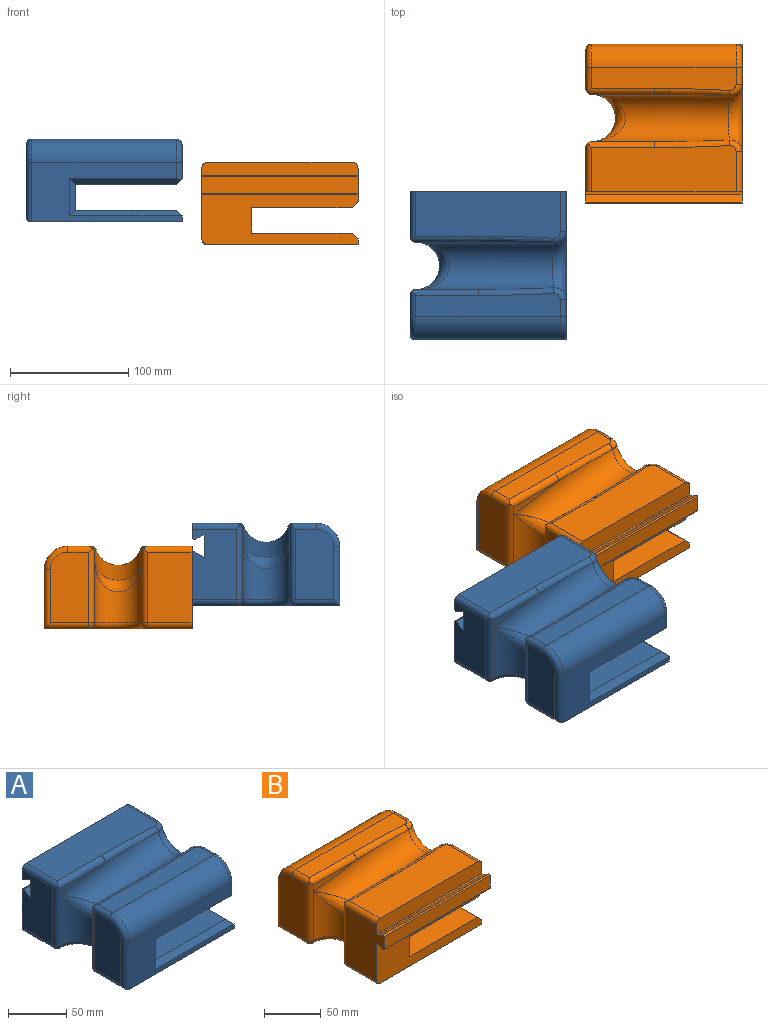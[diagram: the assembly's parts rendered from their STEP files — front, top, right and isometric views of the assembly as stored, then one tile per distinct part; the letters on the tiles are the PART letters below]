
ASSEMBLY  parts=2 mates=1
PART A: 55 faces, bbox 142.1x127.4x74.7 mm
  f0: plane 132x44.75mm, normal (0,1,0), area 3941.6mm2, adj f1,f45,f46,f47,f48,f49,f50,f51
  f1: cylinder r=5mm len=37.5mm, axis (0,1,0), area 294.5mm2, adj f0,f2,f45,f54
  f2: sphere r=5mm, area 39.3mm2, adj f1,f3,f44
  f3: cylinder r=5mm len=63.54mm, axis (0,0,1), area 485.1mm2, adj f2,f4,f41,f42,f43,f54
  f4: cylinder r=5mm len=56.8mm, axis (1,0,0), area 432.2mm2, adj f3,f5,f40,f41,f43
  f5: bspline ~110.14x7.38mm, area 440.2mm2, adj f4,f6,f29,f40
  f6: cylinder r=20mm len=118.3mm, axis (-0.99,0,-0.14), area 5823.8mm2, adj f5,f7,f26,f27,f28,f41
  f7: plane 53.26x7.68mm, normal (0,1,0), area 204.4mm2, adj f6,f8,f25
  f8: cylinder r=5mm len=56.8mm, axis (-1,0,0), area 432.2mm2, adj f7,f9,f24,f25,f26
  f9: plane 122.56x19.77mm, normal (0,0,1), area 2173.6mm2, adj f8,f10,f11,f23,f24,f26
  f10: bspline ~12.78x12.34mm, area 87.4mm2, adj f9,f11,f26,f27
  f11: cylinder r=5mm len=13.91mm, axis (0,1,0), area 109.3mm2, adj f9,f10,f12,f52
  f12: torus R=15mm, axis (1,0,0), area 224.3mm2, adj f11,f13,f23,f52
  f13: cylinder r=5mm len=14.96mm, axis (0,0,-1), area 111.8mm2, adj f12,f14,f17,f51,f52
  f14: plane 94.24x5.7mm, normal (0,-0.71,-0.71), area 632.6mm2, adj f13,f15,f17,f50,f51
  f15: plane 31.5x5mm, normal (0.71,-0.71,0), area 187.4mm2, adj f14,f16,f17,f49
  f16: plane 95x5mm, normal (0,-0.71,0.71), area 636.4mm2, adj f15,f17,f47,f48
  f17: plane 127x50mm, normal (0,-1,0), area 3290mm2, adj f13,f14,f15,f16,f18,f23,f45,f46
  f18: cylinder r=5mm len=50mm, axis (0,0,1), area 373.1mm2, adj f17,f19,f21,f22
  f19: cylinder r=5mm len=37.5mm, axis (0,1,0), area 274.9mm2, adj f18,f20,f21,f45
  f20: sphere r=5mm, area 25mm2, adj f19,f25,f44
  f21: plane 60x32.5mm, normal (-1,0,0), area 1901.7mm2, adj f18,f19,f22,f24,f25
  f22: torus R=15mm, axis (1,0,0), area 224.3mm2, adj f18,f21,f23,f24
  f23: cylinder r=20mm len=122mm, axis (1,0,0), area 3832.7mm2, adj f9,f12,f17,f22
  f24: cylinder r=5mm len=21.04mm, axis (0,-1,0), area 151.3mm2, adj f8,f9,f21,f22,f25
  f25: cylinder r=5mm len=63.54mm, axis (0,0,1), area 485.1mm2, adj f7,f8,f20,f21,f24,f42
  f26: bspline ~63.48x6.36mm, area 440.2mm2, adj f6,f8,f9,f10
  f27: bspline ~57.18x24.11mm, area 968.4mm2, adj f6,f10,f29,f52
  f28: bspline ~40x28.57mm, area 7.5mm2, adj f6,f42
  f29: bspline ~12.78x12.35mm, area 87.4mm2, adj f5,f27,f30,f40
  f30: cylinder r=5mm len=33.91mm, axis (0,1,0), area 266.3mm2, adj f29,f31,f40,f52
  f31: plane 132x13.25mm, normal (0,1,0), area 1738.3mm2, adj f30,f32,f40,f43,f52,f54
  f32: plane 132x1mm, normal (0,0.71,-0.71), area 186.7mm2, adj f31,f33,f52,f54
  f33: plane 132x0.73mm, normal (0,0,-1), area 96.6mm2, adj f32,f34,f52,f54
  f34: cylinder r=1mm len=132mm, axis (-1,0,0), area 69.1mm2, adj f33,f35,f52,f54
  f35: plane 132x8.43mm, normal (0,-0.5,-0.87), area 1284.6mm2, adj f34,f36,f52,f54
  f36: plane 132x20mm, normal (0,1,0), area 2640mm2, adj f35,f37,f52,f54
  f37: plane 132x8.43mm, normal (0,-0.5,0.87), area 1284.6mm2, adj f36,f38,f52,f54
  f38: cylinder r=1mm len=132mm, axis (1,0,0), area 69.1mm2, adj f37,f39,f52,f54
  f39: plane 132x0.73mm, normal (0,0,1), area 96.6mm2, adj f38,f52,f53,f54
  f40: plane 122.56x39.77mm, normal (0,0,1), area 4613.7mm2, adj f4,f5,f29,f30,f31,f43
  f41: plane 53.26x7.68mm, normal (0,-1,0), area 204.4mm2, adj f3,f4,f6
  f42: cylinder r=20mm len=52.32mm, axis (0,0,1), area 2248.2mm2, adj f3,f25,f28,f44
  f43: cylinder r=5mm len=41.04mm, axis (0,-1,0), area 308.4mm2, adj f3,f4,f31,f40,f54
  f44: torus R=25mm, axis (0,0,1), area 538.3mm2, adj f2,f20,f42,f45
  f45: plane 127x125mm, normal (0,0,-1), area 14893.3mm2, adj f0,f1,f17,f19,f44,f46
  f46: plane 125x5mm, normal (1,0,0), area 625mm2, adj f0,f17,f45,f47
  f47: plane 125x5mm, normal (0.71,0,0.71), area 866.2mm2, adj f0,f16,f46,f48
  f48: plane 120x85mm, normal (0,0,1), area 10200mm2, adj f0,f16,f47,f49
  f49: plane 120x21.5mm, normal (1,0,0), area 2580mm2, adj f0,f15,f48,f50
  f50: plane 120x85mm, normal (0,0,-1), area 10200mm2, adj f0,f14,f49,f51
  f51: plane 124.24x5.7mm, normal (0.71,0,-0.71), area 862.4mm2, adj f0,f13,f14,f50,f52
  f52: plane 120x28.5mm, normal (1,0,0), area 2335mm2, adj f0,f11,f12,f13,f27,f30,f31,f32
  f53: plane 132x1mm, normal (0,0.71,0.71), area 186.7mm2, adj f0,f39,f52,f54
  f54: plane 60x37.5mm, normal (-1,0,0), area 2099.1mm2, adj f0,f1,f3,f31,f32,f33,f34,f35
PART B: 53 faces, bbox 142.1x137.4x74.7 mm
  f0: plane 132x46.75mm, normal (0,-1,0), area 4205.6mm2, adj f1,f43,f44,f45,f46,f47,f48,f49
  f1: plane 124.24x5.7mm, normal (0.71,0,-0.71), area 862.4mm2, adj f0,f2,f42,f43,f52
  f2: cylinder r=5mm len=14.96mm, axis (0,0,1), area 111.8mm2, adj f1,f3,f39,f42,f52
  f3: torus R=15mm, axis (1,0,0), area 224.3mm2, adj f2,f4,f38,f52
  f4: cylinder r=5mm len=13.91mm, axis (0,1,0), area 109.3mm2, adj f3,f5,f37,f52
  f5: bspline ~12.78x12.35mm, area 87.4mm2, adj f4,f6,f36,f37
  f6: bspline ~57.18x24.11mm, area 968.4mm2, adj f5,f7,f35,f52
  f7: bspline ~12.78x12.34mm, area 87.4mm2, adj f6,f8,f33,f34
  f8: plane 122.56x39.77mm, normal (0,0,1), area 4613.6mm2, adj f7,f9,f16,f32,f33,f34
  f9: plane 132x15.25mm, normal (0,-1,0), area 2002.3mm2, adj f8,f10,f16,f34,f50,f52
  f10: plane 132x2mm, normal (0,0,1), area 264mm2, adj f9,f11,f50,f52
  f11: plane 132x6.5mm, normal (0,0.5,0.87), area 990.7mm2, adj f10,f12,f50,f52
  f12: cylinder r=1mm len=132mm, axis (-1,0,0), area 276.5mm2, adj f11,f13,f50,f52
  f13: plane 132x13.77mm, normal (0,-1,0), area 1818.1mm2, adj f12,f14,f50,f52
  f14: cylinder r=1mm len=132mm, axis (-1,0,0), area 276.5mm2, adj f13,f15,f50,f52
  f15: plane 132x6.5mm, normal (0,0.5,-0.87), area 990.7mm2, adj f14,f50,f51,f52
  f16: cylinder r=5mm len=41.04mm, axis (0,-1,0), area 308.4mm2, adj f8,f9,f17,f32,f50
  f17: cylinder r=5mm len=63.54mm, axis (0,0,1), area 485.1mm2, adj f16,f18,f29,f31,f32,f50
  f18: sphere r=5mm, area 25mm2, adj f17,f19,f49
  f19: torus R=25mm, axis (0,0,1), area 538.3mm2, adj f18,f20,f29,f48
  f20: sphere r=5mm, area 39.3mm2, adj f19,f21,f28
  f21: cylinder r=5mm len=37.5mm, axis (0,1,0), area 274.9mm2, adj f20,f22,f27,f48
  f22: cylinder r=5mm len=50mm, axis (0,0,-1), area 373.1mm2, adj f21,f23,f27,f39
  f23: torus R=15mm, axis (1,0,0), area 224.3mm2, adj f22,f24,f27,f38
  f24: cylinder r=5mm len=21.04mm, axis (0,-1,0), area 151.3mm2, adj f23,f25,f27,f28,f37
  f25: cylinder r=5mm len=56.8mm, axis (1,0,0), area 432.2mm2, adj f24,f26,f28,f36,f37
  f26: plane 53.26x7.68mm, normal (0,-1,0), area 204.4mm2, adj f25,f28,f35
  f27: plane 60x32.5mm, normal (-1,0,0), area 1901.7mm2, adj f21,f22,f23,f24,f28
  f28: cylinder r=5mm len=63.54mm, axis (0,0,1), area 485.1mm2, adj f20,f24,f25,f26,f27,f29
  f29: cylinder r=20mm len=52.32mm, axis (0,0,1), area 2248.2mm2, adj f17,f19,f28,f30
  f30: bspline ~40x28.57mm, area 7.5mm2, adj f29,f35
  f31: plane 53.26x7.68mm, normal (0,1,0), area 204.4mm2, adj f17,f32,f35
  f32: cylinder r=5mm len=56.8mm, axis (-1,0,0), area 432.2mm2, adj f8,f16,f17,f31,f33
  f33: bspline ~63.48x6.36mm, area 440.2mm2, adj f7,f8,f32,f35
  f34: cylinder r=5mm len=33.91mm, axis (0,1,0), area 266.3mm2, adj f7,f8,f9,f52
  f35: cylinder r=20mm len=118.3mm, axis (-0.99,0,-0.14), area 5823.8mm2, adj f6,f26,f30,f31,f33,f36
  f36: bspline ~110.14x7.38mm, area 440.2mm2, adj f5,f25,f35,f37
  f37: plane 122.56x19.77mm, normal (0,0,1), area 2173.7mm2, adj f4,f5,f24,f25,f36,f38
  f38: cylinder r=20mm len=122mm, axis (-1,0,0), area 3832.7mm2, adj f3,f23,f37,f39
  f39: plane 127x50mm, normal (0,1,0), area 3290mm2, adj f2,f22,f38,f40,f41,f42,f47,f48
  f40: plane 95x5mm, normal (0,0.71,0.71), area 636.4mm2, adj f39,f41,f45,f46
  f41: plane 31.5x5mm, normal (0.71,0.71,0), area 187.4mm2, adj f39,f40,f42,f44
  f42: plane 94.24x5.7mm, normal (0,0.71,-0.71), area 632.6mm2, adj f1,f2,f39,f41,f43
  f43: plane 120x85mm, normal (0,0,-1), area 10200mm2, adj f0,f1,f42,f44
  f44: plane 120x21.5mm, normal (1,0,0), area 2580mm2, adj f0,f41,f43,f45
  f45: plane 120x85mm, normal (0,0,1), area 10200mm2, adj f0,f40,f44,f46
  f46: plane 125x5mm, normal (0.71,0,0.71), area 866.2mm2, adj f0,f40,f45,f47
  f47: plane 125x5mm, normal (1,0,0), area 625mm2, adj f0,f39,f46,f48
  f48: plane 127x125mm, normal (0,0,-1), area 14893.3mm2, adj f0,f19,f21,f39,f47,f49
  f49: cylinder r=5mm len=37.5mm, axis (0,1,0), area 294.5mm2, adj f0,f18,f48,f50
  f50: plane 60x47.5mm, normal (-1,0,0), area 2365.6mm2, adj f0,f9,f10,f11,f12,f13,f14,f15
  f51: plane 132x2mm, normal (0,0,-1), area 264mm2, adj f0,f15,f50,f52
  f52: plane 130x28.5mm, normal (1,0,0), area 2601.5mm2, adj f0,f1,f2,f3,f4,f6,f9,f10
PLACE A t=(20,62.5,40)mm
PLACE B t=(168.69,187.5,20.55)mm
MATE planar B.f0 <-> A.f0  axis (0,-1,0) through (185.69,125,12.05)mm
